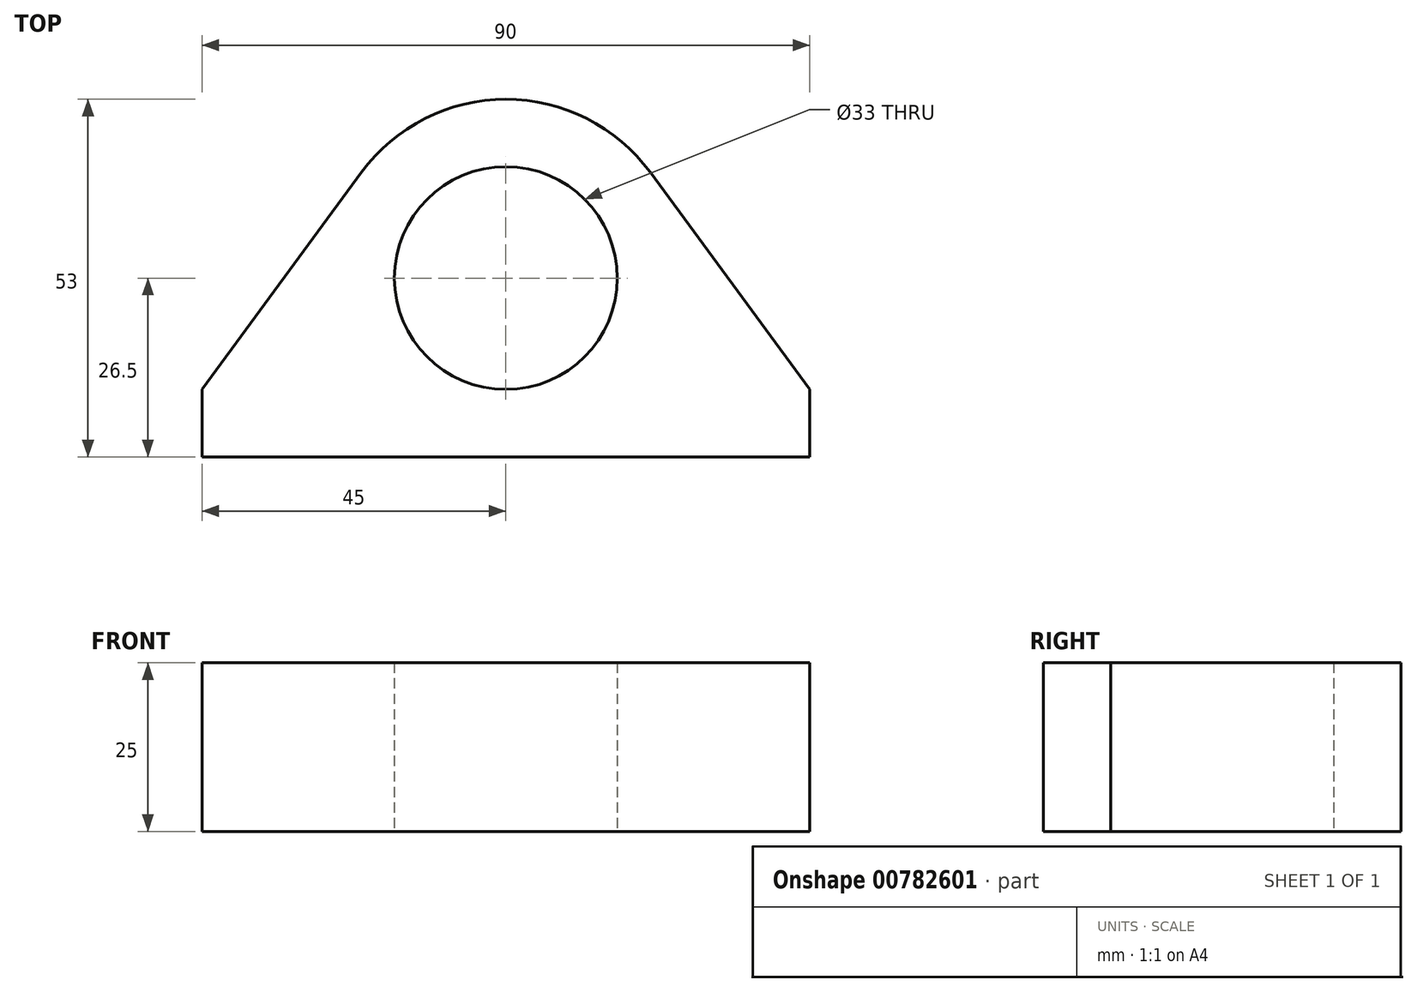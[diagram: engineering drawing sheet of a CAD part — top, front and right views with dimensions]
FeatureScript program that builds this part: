
annotation { "Feature Type Name" : "Feature", "Feature Type Description" : "" }
export const myFeature = defineFeature(function(context is Context, id is Id, definition is map)
    precondition{}
    {
        {
            var Q0;
            Q0=qCreatedBy(makeId("Top.planeOp"),FACE);
            var sketch = newSketch(context, id + "F0", { "sketchPlane" : qUnion([Q0])});
            skCircle(sketch, "E0", {"center": v(0, 0) * mm, "radius": 16.5 * mm});
            skCircle(sketch, "E1.0", {"center": v(0, 0) * mm, "radius": 26.5 * mm});
            skLineSegment(sketch, "E2.bottom", {"start": v(0, -16.5) * mm, "end": v(45, -16.5) * mm});
            skLineSegment(sketch, "E2.top", {"start": v(0, -26.5) * mm, "end": v(45, -26.5) * mm});
            skLineSegment(sketch, "E2.left", {"start": v(0, -16.5) * mm, "end": v(0, -26.5) * mm});
            skLineSegment(sketch, "E2.right", {"start": v(45, -16.5) * mm, "end": v(45, -26.5) * mm});
            skLineSegment(sketch, "E3.bottom", {"start": v(0, -16.5) * mm, "end": v(-45, -16.5) * mm});
            skLineSegment(sketch, "E3.top", {"start": v(0, -26.5) * mm, "end": v(-45, -26.5) * mm});
            skLineSegment(sketch, "E3.right", {"start": v(-45, -16.5) * mm, "end": v(-45, -26.5) * mm});
            skLineSegment(sketch, "E4", {"start": v(-45, -16.5) * mm, "end": v(-21.36, 15.69) * mm});
            skLineSegment(sketch, "E5", {"start": v(45, -16.5) * mm, "end": v(21.36, 15.69) * mm});
            skSolve(sketch);
        }
        {
            var Q0;
            Q0 = qSketchRegion(id + "F0", true);
            extrude(context, id + "F1", {"entities" : qUnion([Q0]), "depth" : 25 * mm, "offsetDistance" : 25 * mm});
        }
    });
